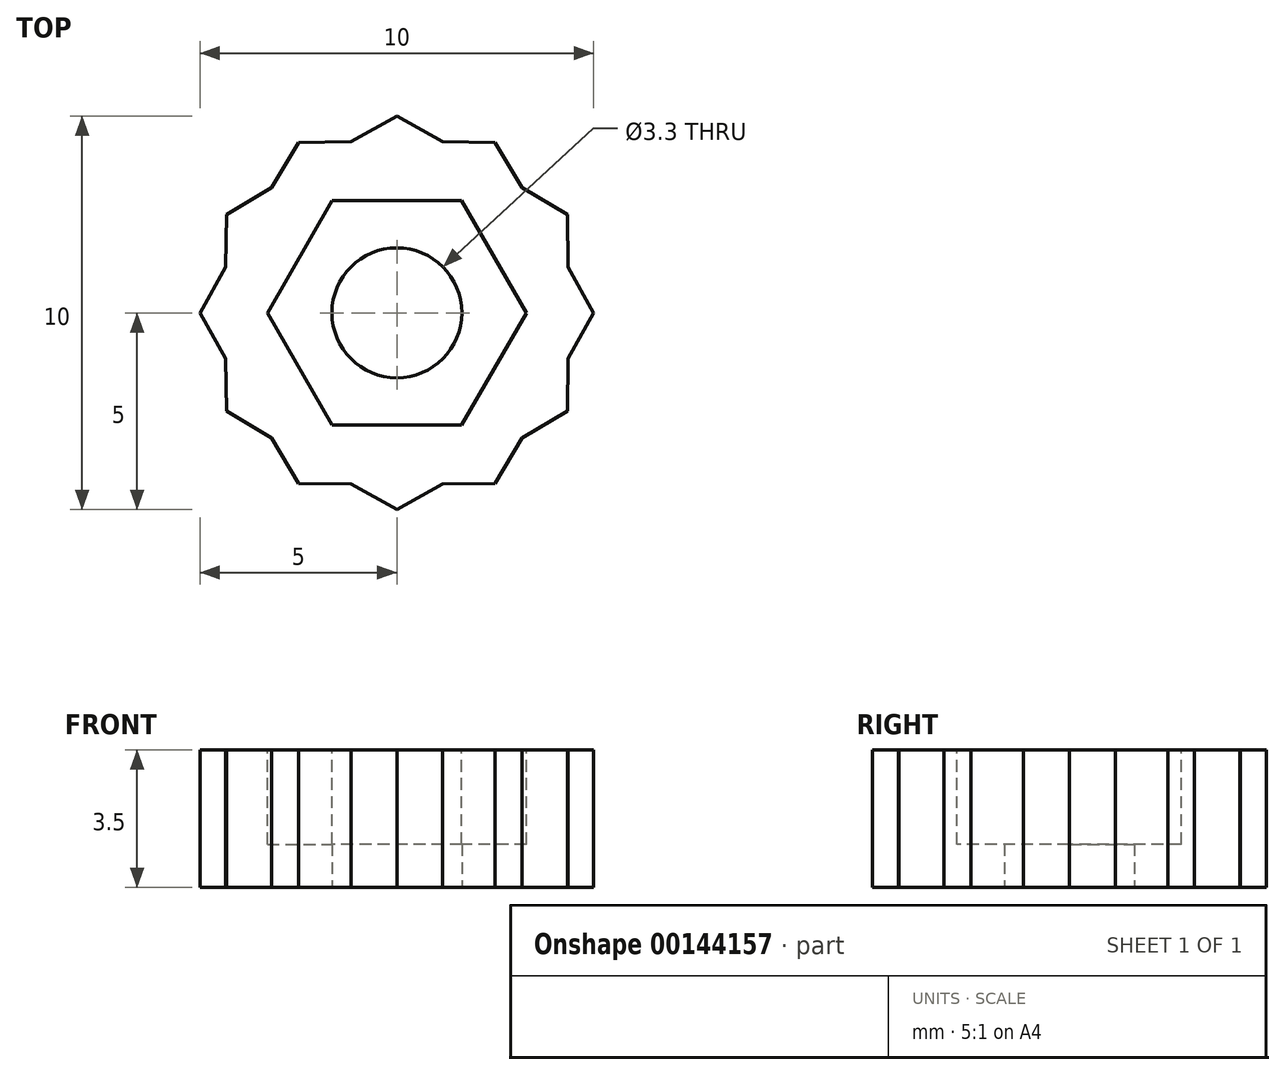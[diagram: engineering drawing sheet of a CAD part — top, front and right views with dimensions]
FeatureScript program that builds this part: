
annotation { "Feature Type Name" : "Feature", "Feature Type Description" : "" }
export const myFeature = defineFeature(function(context is Context, id is Id, definition is map)
    precondition{}
    {
        {
            var Q0;
            Q0=qCreatedBy(makeId("Top.planeOp"),FACE);
            var sketch = newSketch(context, id + "F0", { "sketchPlane" : qUnion([Q0])});
            skCircle(sketch, "E0", {"center": v(0, 0) * mm, "radius": 4.5 * mm, "construction": true});
            skLineSegment(sketch, "E1", {"start": v(0, 0) * mm, "end": v(-1.16, 4.35) * mm, "construction": true});
            skLineSegment(sketch, "E2", {"start": v(-1.16, 4.35) * mm, "end": v(0, 5) * mm});
            skLineSegment(sketch, "E3", {"start": v(0, 5) * mm, "end": v(1.16, 4.35) * mm});
            skLineSegment(sketch, "E4", {"start": v(1.16, 4.35) * mm, "end": v(0, 0) * mm, "construction": true});
            skLineSegment(sketch, "E5", {"start": v(0, 5) * mm, "end": v(0, 4.5) * mm});
            skLineSegment(sketch, "E6.1.0", {"start": v(-2.5, 4.33) * mm, "end": v(-1.16, 4.35) * mm});
            skLineSegment(sketch, "E6.1.1", {"start": v(-3.18, 3.18) * mm, "end": v(-2.5, 4.33) * mm});
            skLineSegment(sketch, "E7.3.2.0", {"start": v(-4.35, 1.16) * mm, "end": v(-4.33, 2.5) * mm});
            skLineSegment(sketch, "E7.4.2.0", {"start": v(-4.33, 2.5) * mm, "end": v(-3.18, 3.18) * mm});
            skLineSegment(sketch, "E7.3.3.0", {"start": v(-4.35, -1.16) * mm, "end": v(-5, 0) * mm});
            skLineSegment(sketch, "E7.4.3.0", {"start": v(-5, 0) * mm, "end": v(-4.35, 1.16) * mm});
            skLineSegment(sketch, "E7.3.4.0", {"start": v(-3.18, -3.18) * mm, "end": v(-4.33, -2.5) * mm});
            skLineSegment(sketch, "E7.4.4.0", {"start": v(-4.33, -2.5) * mm, "end": v(-4.35, -1.16) * mm});
            skLineSegment(sketch, "E7.3.5.0", {"start": v(-1.16, -4.35) * mm, "end": v(-2.5, -4.33) * mm});
            skLineSegment(sketch, "E7.4.5.0", {"start": v(-2.5, -4.33) * mm, "end": v(-3.18, -3.18) * mm});
            skLineSegment(sketch, "E7.3.6.0", {"start": v(1.16, -4.35) * mm, "end": v(0, -5) * mm});
            skLineSegment(sketch, "E7.4.6.0", {"start": v(0, -5) * mm, "end": v(-1.16, -4.35) * mm});
            skLineSegment(sketch, "E7.3.7.0", {"start": v(3.18, -3.18) * mm, "end": v(2.5, -4.33) * mm});
            skLineSegment(sketch, "E7.4.7.0", {"start": v(2.5, -4.33) * mm, "end": v(1.16, -4.35) * mm});
            skLineSegment(sketch, "E7.3.8.0", {"start": v(4.35, -1.16) * mm, "end": v(4.33, -2.5) * mm});
            skLineSegment(sketch, "E7.4.8.0", {"start": v(4.33, -2.5) * mm, "end": v(3.18, -3.18) * mm});
            skLineSegment(sketch, "E7.3.9.0", {"start": v(4.35, 1.16) * mm, "end": v(5, 0) * mm});
            skLineSegment(sketch, "E7.4.9.0", {"start": v(5, 0) * mm, "end": v(4.35, -1.16) * mm});
            skLineSegment(sketch, "E8.3.10.0", {"start": v(3.18, 3.18) * mm, "end": v(4.33, 2.5) * mm});
            skLineSegment(sketch, "E8.4.10.0", {"start": v(4.33, 2.5) * mm, "end": v(4.35, 1.16) * mm});
            skLineSegment(sketch, "E9.3.11.0", {"start": v(1.16, 4.35) * mm, "end": v(2.5, 4.33) * mm});
            skLineSegment(sketch, "E9.4.11.0", {"start": v(2.5, 4.33) * mm, "end": v(3.18, 3.18) * mm});
            skSolve(sketch);
        }
        {
            var Q0;
            Q0=makeQuery(id+"F0.imprint","IMPRINT",FACE,{"disambiguationData":[TD([[makeQuery(id+"F0.imprint","IMPRINT",EDGE,{"derivedFrom":sQuery(id+"F0.wireOp",EDGE,"E2")}),-1.0]])]});
            var Q1;
            Q1=sQuery(id+"F0.wireOp",EDGE,"E6.2.0");
            var Q2;
            Q2=sQuery(id+"F0.wireOp",EDGE,"E0");
            extrude(context, id + "F1", {"entities" : qUnion([Q0]), "surfaceEntities" : qUnion([Q1, Q2]), "depth" : 3.5 * mm});
        }
        {
            var Q0;
            Q0=makeQuery(id+"F1.opExtrude","CAP_FACE",FACE,{"disambiguationData":[OSD([sQuery(id+"F0.wireOp",EDGE,"E2"),sQuery(id+"F0.wireOp",EDGE,"E3"),sQuery(id+"F0.wireOp",EDGE,"E6.1.0"),sQuery(id+"F0.wireOp",EDGE,"E6.1.1"),sQuery(id+"F0.wireOp",EDGE,"E7.3.2.0"),sQuery(id+"F0.wireOp",EDGE,"E7.4.2.0"),sQuery(id+"F0.wireOp",EDGE,"E7.3.3.0"),sQuery(id+"F0.wireOp",EDGE,"E7.4.3.0"),sQuery(id+"F0.wireOp",EDGE,"E7.3.4.0"),sQuery(id+"F0.wireOp",EDGE,"E7.4.4.0"),sQuery(id+"F0.wireOp",EDGE,"E7.3.5.0"),sQuery(id+"F0.wireOp",EDGE,"E7.4.5.0"),sQuery(id+"F0.wireOp",EDGE,"E7.3.6.0"),sQuery(id+"F0.wireOp",EDGE,"E7.4.6.0"),sQuery(id+"F0.wireOp",EDGE,"E7.3.7.0"),sQuery(id+"F0.wireOp",EDGE,"E7.4.7.0"),sQuery(id+"F0.wireOp",EDGE,"E7.3.8.0"),sQuery(id+"F0.wireOp",EDGE,"E7.4.8.0"),sQuery(id+"F0.wireOp",EDGE,"E7.3.9.0"),sQuery(id+"F0.wireOp",EDGE,"E7.4.9.0"),sQuery(id+"F0.wireOp",EDGE,"E8.3.10.0"),sQuery(id+"F0.wireOp",EDGE,"E8.4.10.0"),sQuery(id+"F0.wireOp",EDGE,"E9.3.11.0"),sQuery(id+"F0.wireOp",EDGE,"E9.4.11.0")])],"isStart":false});
            var sketch = newSketch(context, id + "F2", { "sketchPlane" : qUnion([Q0])});
            skCircle(sketch, "E10.cCircle", {"center": v(0, 0) * mm, "radius": 3.3 * mm, "construction": true});
            skLineSegment(sketch, "E10.0", {"start": v(1.65, -2.85) * mm, "end": v(-1.65, -2.85) * mm});
            skLineSegment(sketch, "E10.1", {"start": v(-1.65, -2.85) * mm, "end": v(-3.3, 0) * mm});
            skLineSegment(sketch, "E10.2", {"start": v(-3.3, 0) * mm, "end": v(-1.65, 2.85) * mm});
            skLineSegment(sketch, "E10.3", {"start": v(-1.65, 2.85) * mm, "end": v(1.65, 2.85) * mm});
            skLineSegment(sketch, "E10.4", {"start": v(1.65, 2.85) * mm, "end": v(3.3, 0) * mm});
            skLineSegment(sketch, "E10.5", {"start": v(3.3, 0) * mm, "end": v(1.65, -2.85) * mm});
            skSolve(sketch);
        }
        {
            var Q0;
            Q0 = qSketchRegion(id + "F2", true);
            extrude(context, id + "F3", {"entities" : qUnion([Q0]), "operationType" : NewBodyOperationType.REMOVE, "oppositeDirection" : true, "depth" : 2.4 * mm});
        }
        {
            var Q0;
            Q0=sQuery(id+"F0.wireOp",VERTEX,"E0.center");
            var Q1;
            Q1=makeQuery(id+"F1.opExtrude","SWEPT_BODY",BODY,{"disambiguationData":[OSD([sQuery(id+"F0.wireOp",EDGE,"E2"),sQuery(id+"F0.wireOp",EDGE,"E3"),sQuery(id+"F0.wireOp",EDGE,"E6.1.0"),sQuery(id+"F0.wireOp",EDGE,"E6.1.1"),sQuery(id+"F0.wireOp",EDGE,"E7.3.2.0"),sQuery(id+"F0.wireOp",EDGE,"E7.4.2.0"),sQuery(id+"F0.wireOp",EDGE,"E7.3.3.0"),sQuery(id+"F0.wireOp",EDGE,"E7.4.3.0"),sQuery(id+"F0.wireOp",EDGE,"E7.3.4.0"),sQuery(id+"F0.wireOp",EDGE,"E7.4.4.0"),sQuery(id+"F0.wireOp",EDGE,"E7.3.5.0"),sQuery(id+"F0.wireOp",EDGE,"E7.4.5.0"),sQuery(id+"F0.wireOp",EDGE,"E7.3.6.0"),sQuery(id+"F0.wireOp",EDGE,"E7.4.6.0"),sQuery(id+"F0.wireOp",EDGE,"E7.3.7.0"),sQuery(id+"F0.wireOp",EDGE,"E7.4.7.0"),sQuery(id+"F0.wireOp",EDGE,"E7.3.8.0"),sQuery(id+"F0.wireOp",EDGE,"E7.4.8.0"),sQuery(id+"F0.wireOp",EDGE,"E7.3.9.0"),sQuery(id+"F0.wireOp",EDGE,"E7.4.9.0"),sQuery(id+"F0.wireOp",EDGE,"E8.3.10.0"),sQuery(id+"F0.wireOp",EDGE,"E8.4.10.0"),sQuery(id+"F0.wireOp",EDGE,"E9.3.11.0"),sQuery(id+"F0.wireOp",EDGE,"E9.4.11.0")])]});
            hole(context, id + "F4", {"style" : HoleStyle.SIMPLE, "endStyle" : HoleEndStyle.THROUGH, "oppositeDirection" : true, "standardTappedOrClearance" : lookupTablePath({ "standard" : "ISO", "fit" : "Normal", "size" : "M3", "type" : "Clearance" }), "standardBlindInLast" : lookupTablePath({ "fit" : "Standard", "standard" : "ISO", "size" : "M3", "type" : "Clearance" }), "holeDiameter" : 3.3 * mm, "startFromSketch" : true, "locations" : qUnion([Q0]), "scope" : qUnion([Q1]), "isTappedThrough" : true});
        }
    });
